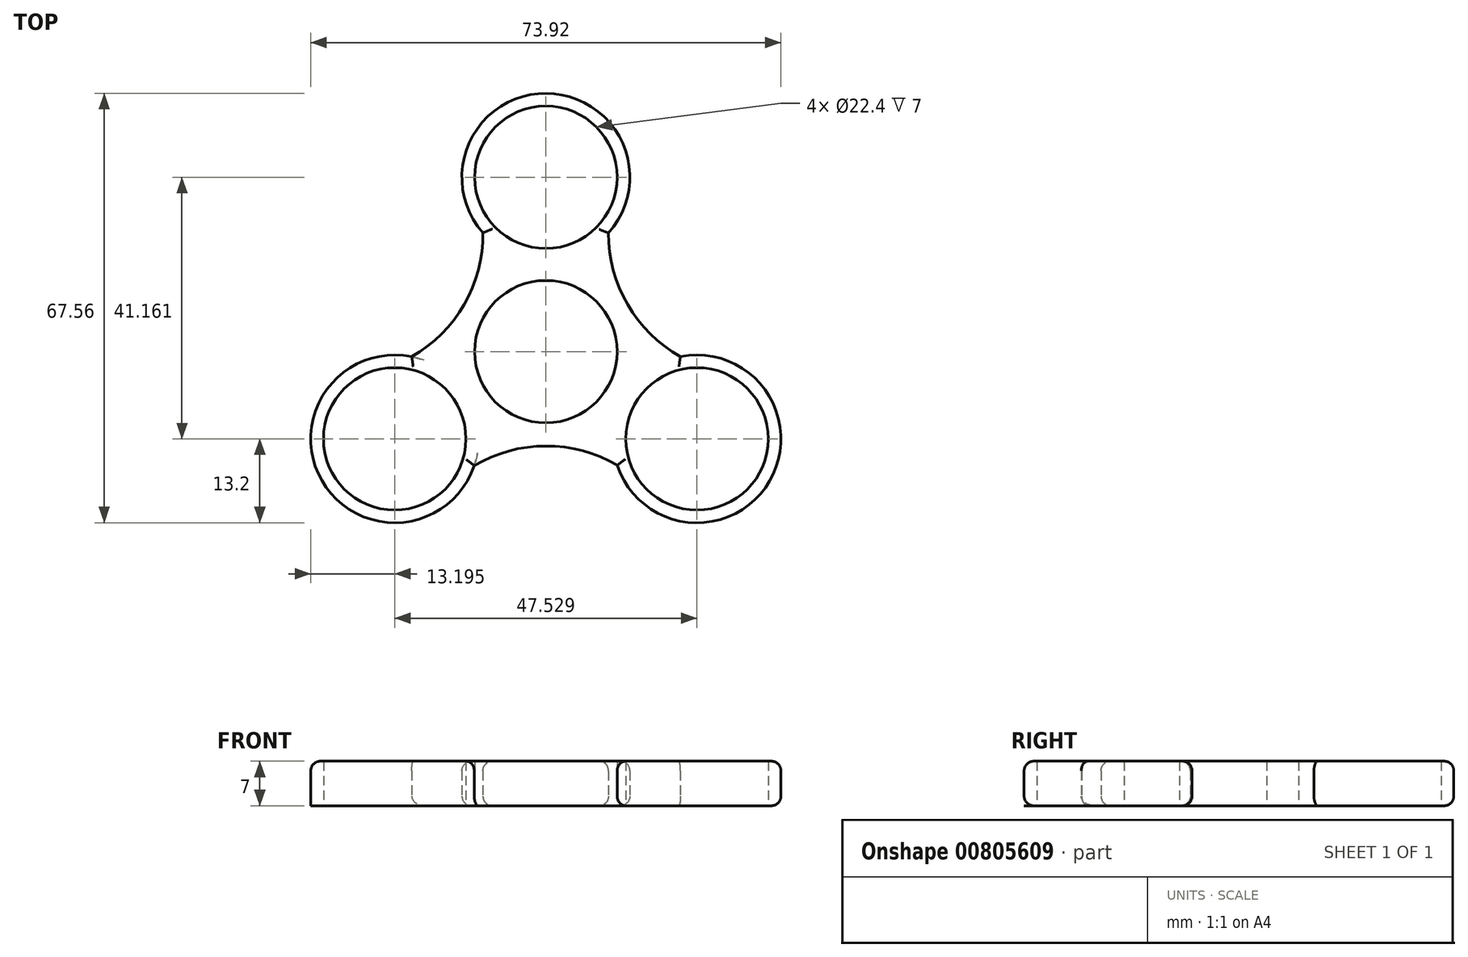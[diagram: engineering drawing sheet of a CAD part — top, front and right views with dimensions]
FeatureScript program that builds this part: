
annotation { "Feature Type Name" : "Feature", "Feature Type Description" : "" }
export const myFeature = defineFeature(function(context is Context, id is Id, definition is map)
    precondition{}
    {
        {
            var Q0;
            Q0=qCreatedBy(makeId("Top.planeOp"),FACE);
            var sketch = newSketch(context, id + "F0", { "sketchPlane" : qUnion([Q0])});
            skCircle(sketch, "E0", {"center": v(0, 0) * mm, "radius": 11.2 * mm});
            skSolve(sketch);
        }
        {
            var Q0;
            Q0=makeQuery(id+"F0.imprint","IMPRINT",FACE,{"disambiguationData":[TD([[makeQuery(id+"F0.imprint","IMPRINT",EDGE,{"derivedFrom":sQuery(id+"F0.wireOp",EDGE,"E0")}),1.0]])]});
            var sketch = newSketch(context, id + "F1", { "sketchPlane" : qUnion([Q0])});
            skCircle(sketch, "E1", {"center": v(0, 27.44) * mm, "radius": 11.2 * mm});
            skArc(sketch, "E2", {"start": v(9.85, 18.66) * mm, "mid": v(0.03, 40.64) * mm, "end": v(-9.9, 18.7) * mm});
            skArc(sketch, "E3.1.0", {"start": v(-21.09, -0.8) * mm, "mid": v(-35.21, -20.3) * mm, "end": v(-11.25, -17.93) * mm});
            skCircle(sketch, "E3.1.1", {"center": v(-23.76, -13.72) * mm, "radius": 11.2 * mm});
            skArc(sketch, "E3.2.0", {"start": v(11.23, -17.86) * mm, "mid": v(35.18, -20.35) * mm, "end": v(21.15, -0.78) * mm});
            skCircle(sketch, "E3.2.1", {"center": v(23.76, -13.72) * mm, "radius": 11.2 * mm});
            skPoint(sketch, "E3.center", {"position": v(0, 0) * mm});
            skArc(sketch, "E4", {"start": v(9.85, 18.66) * mm, "mid": v(12.86, 7.4) * mm, "end": v(21.15, -0.78) * mm});
            skArc(sketch, "E5.1.0", {"start": v(-21.09, -0.8) * mm, "mid": v(-12.84, 7.44) * mm, "end": v(-9.9, 18.7) * mm});
            skArc(sketch, "E5.2.0", {"start": v(11.23, -17.86) * mm, "mid": v(-0.02, -14.84) * mm, "end": v(-11.25, -17.93) * mm});
            skPoint(sketch, "E6.orphan", {"position": v(48.74, 27.44) * mm});
            skSolve(sketch);
        }
        {
            var Q0;
            Q0=makeQuery(id+"F1.imprint","IMPRINT",FACE,{"disambiguationData":[TD([[makeQuery(id+"F1.imprint","IMPRINT",EDGE,{"derivedFrom":sQuery(id+"F1.wireOp",EDGE,"E1")}),-1.0]])]});
            extrude(context, id + "F2", {"entities" : qUnion([Q0]), "depth" : 7 * mm, "offsetDistance" : 25 * mm});
        }
        {
            var Q0;
            Q0=makeQuery(id+"F2.opExtrude","CAP_EDGE",EDGE,{"disambiguationData":[OSD([sQuery(id+"F1.wireOp",EDGE,"E5.2.0")])],"isStart":true});
            fillet(context, id + "F3", {"entities" : qUnion([Q0]), "radius" : 1.5 * mm, "tangentPropagation" : true, "allowEdgeOverflow" : false});
        }
        {
            var Q0;
            Q0=makeQuery(id+"F2.opExtrude","CAP_EDGE",EDGE,{"disambiguationData":[OSD([sQuery(id+"F1.wireOp",EDGE,"E3.1.0")])],"isStart":false});
            var Q1;
            Q1=makeQuery(id+"F2.opExtrude","CAP_EDGE",EDGE,{"disambiguationData":[OSD([sQuery(id+"F1.wireOp",EDGE,"E5.2.0")])],"isStart":false});
            var Q2;
            Q2=makeQuery(id+"F2.opExtrude","CAP_EDGE",EDGE,{"disambiguationData":[OSD([sQuery(id+"F1.wireOp",EDGE,"E5.1.0")])],"isStart":false});
            var Q3;
            Q3=makeQuery(id+"F2.opExtrude","CAP_EDGE",EDGE,{"disambiguationData":[OSD([sQuery(id+"F1.wireOp",EDGE,"E2")])],"isStart":false});
            var Q4;
            Q4=makeQuery(id+"F2.opExtrude","CAP_EDGE",EDGE,{"disambiguationData":[OSD([sQuery(id+"F1.wireOp",EDGE,"E3.2.0")])],"isStart":false});
            var Q5;
            Q5=makeQuery(id+"F2.opExtrude","CAP_EDGE",EDGE,{"disambiguationData":[OSD([sQuery(id+"F1.wireOp",EDGE,"E4")])],"isStart":false});
            var Q6;
            {var subQ0=sQuery(id+"F1.wireOp",EDGE,"E5.2.0");Q6=makeQuery(id+"F3.opFillet","BLEND_EDGE",EDGE,{"blendedFrom":[makeQuery(id+"F2.opExtrude","CAP_EDGE",EDGE,{"disambiguationData":[OSD([subQ0])],"isStart":true}),makeQuery(id+"F2.opExtrude","SWEPT_FACE",FACE,{"disambiguationData":[OSD([subQ0])]})],"blendedInto":[makeQuery(id+"F2.opExtrude","SWEPT_FACE",FACE,{"disambiguationData":[OSD([subQ0])]})]});}
            fillet(context, id + "F4", {"entities" : qUnion([Q0, Q1, Q2, Q3, Q4, Q5, Q6]), "radius" : 1.5 * mm, "tangentPropagation" : true, "allowEdgeOverflow" : false});
        }
        {
            var Q0;
            Q0=makeQuery(id+"F2.opExtrude","CAP_EDGE",EDGE,{"disambiguationData":[OSD([sQuery(id+"F1.wireOp",EDGE,"E3.2.0")])],"isStart":true});
            var Q1;
            Q1=makeQuery(id+"F2.opExtrude","CAP_EDGE",EDGE,{"disambiguationData":[OSD([sQuery(id+"F1.wireOp",EDGE,"E2")])],"isStart":true});
            var Q2;
            Q2=makeQuery(id+"F2.opExtrude","CAP_EDGE",EDGE,{"disambiguationData":[OSD([sQuery(id+"F1.wireOp",EDGE,"E5.1.0")])],"isStart":true});
            var Q3;
            {var subQ0=sQuery(id+"F1.wireOp",EDGE,"E3.1.0");Q3=makeQuery(id+"F4.opFillet","BLEND_EDGE",EDGE,{"blendedFrom":[makeQuery(id+"F2.opExtrude","CAP_EDGE",EDGE,{"disambiguationData":[OSD([subQ0])],"isStart":false}),makeQuery(id+"F2.opExtrude","SWEPT_FACE",FACE,{"disambiguationData":[OSD([subQ0])]})],"blendedInto":[makeQuery(id+"F2.opExtrude","SWEPT_FACE",FACE,{"disambiguationData":[OSD([subQ0])]})]});}
            var Q4;
            {var subQ0=sQuery(id+"F1.wireOp",EDGE,"E5.2.0");Q4=makeQuery(id+"F3.opFillet","BLEND_EDGE",EDGE,{"blendedFrom":[makeQuery(id+"F2.opExtrude","CAP_EDGE",EDGE,{"disambiguationData":[OSD([subQ0])],"isStart":true}),makeQuery(id+"F2.opExtrude","CAP_FACE",FACE,{"disambiguationData":[OSD([sQuery(id+"F0.wireOp",EDGE,"E0"),sQuery(id+"F1.wireOp",EDGE,"E1"),sQuery(id+"F1.wireOp",EDGE,"E2"),sQuery(id+"F1.wireOp",EDGE,"E3.1.0"),sQuery(id+"F1.wireOp",EDGE,"E3.1.1"),sQuery(id+"F1.wireOp",EDGE,"E3.2.0"),sQuery(id+"F1.wireOp",EDGE,"E3.2.1"),sQuery(id+"F1.wireOp",EDGE,"E4"),sQuery(id+"F1.wireOp",EDGE,"E5.1.0"),subQ0])],"isStart":true})],"blendedInto":[makeQuery(id+"F2.opExtrude","CAP_FACE",FACE,{"disambiguationData":[OSD([sQuery(id+"F0.wireOp",EDGE,"E0"),sQuery(id+"F1.wireOp",EDGE,"E1"),sQuery(id+"F1.wireOp",EDGE,"E2"),sQuery(id+"F1.wireOp",EDGE,"E3.1.0"),sQuery(id+"F1.wireOp",EDGE,"E3.1.1"),sQuery(id+"F1.wireOp",EDGE,"E3.2.0"),sQuery(id+"F1.wireOp",EDGE,"E3.2.1"),sQuery(id+"F1.wireOp",EDGE,"E4"),sQuery(id+"F1.wireOp",EDGE,"E5.1.0"),subQ0])],"isStart":true})]});}
            fillet(context, id + "F5", {"entities" : qUnion([Q0, Q1, Q2, Q3, Q4]), "radius" : 1.5 * mm, "tangentPropagation" : true, "allowEdgeOverflow" : false});
        }
        {
            var Q0;
            Q0=makeQuery(id+"F2.opExtrude","CAP_EDGE",EDGE,{"disambiguationData":[OSD([sQuery(id+"F1.wireOp",EDGE,"E4")])],"isStart":true});
            fillet(context, id + "F6", {"entities" : qUnion([Q0]), "radius" : 1.5 * mm, "tangentPropagation" : true, "allowEdgeOverflow" : false});
        }
    });
